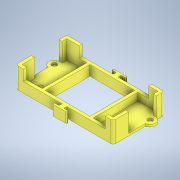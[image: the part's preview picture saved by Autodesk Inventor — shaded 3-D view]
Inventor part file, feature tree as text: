
AUTODESK INVENTOR PART (.ipt)
format: ipt  version: 2022 (Build 260153000, 153)  size: 260,096 bytes
history: native  units: mm
features: extrude x5, fillet x2, other x1, sketch x1
ambient origin geometry x8: Origin, YZ Plane, XZ Plane, XY Plane, X Axis, Y Axis, Z Axis, Center Point
bodies: Body1 (feature_tree)
feature tree (9):
  other  "ソリッド1"
  sketch  "スケッチ1"
  extrude  "ベース"  Depth=23.0mm
  extrude  "囲い柱"  Depth=31.0mm
  extrude  "底上げ"  Depth=3.2mm
  extrude  "肉抜き"  Depth=59.0mm
  extrude  "輪ゴムタブ"  Depth=29.0mm
  fillet  "フィレット1"  Radius=7.0mm
  fillet  "フィレット2"  Radius=2.0mm
